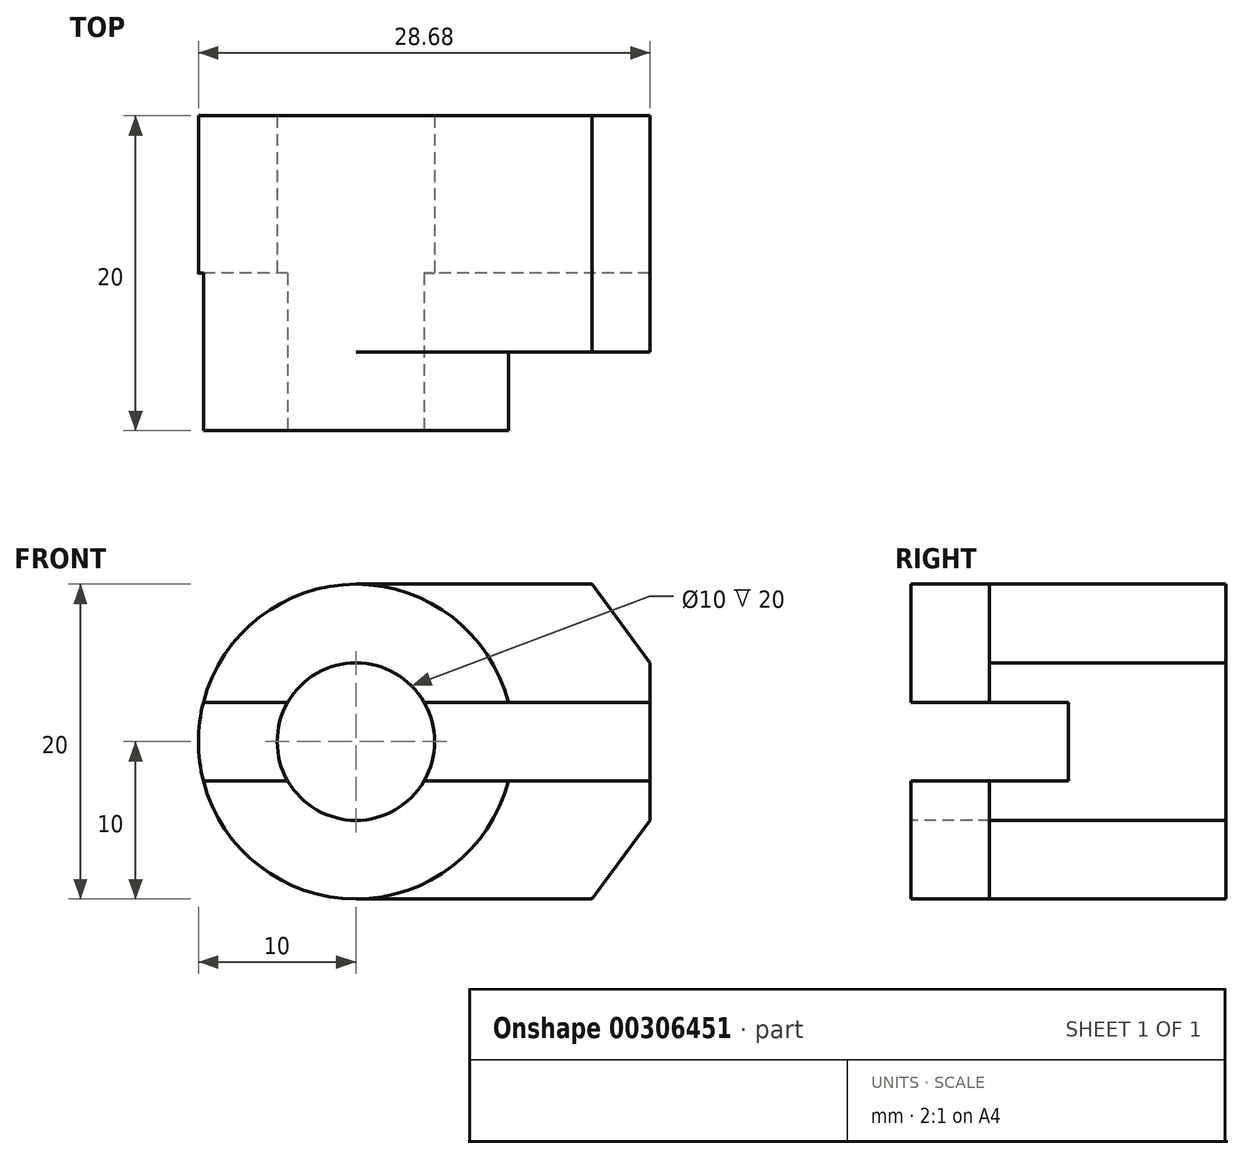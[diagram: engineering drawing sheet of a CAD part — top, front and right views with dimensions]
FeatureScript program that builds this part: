
annotation { "Feature Type Name" : "Feature", "Feature Type Description" : "" }
export const myFeature = defineFeature(function(context is Context, id is Id, definition is map)
    precondition{}
    {
        {
            var Q0;
            Q0=qCreatedBy(makeId("Front.planeOp"),FACE);
            var sketch = newSketch(context, id + "F0", { "sketchPlane" : qUnion([Q0])});
            skCircle(sketch, "E0", {"center": v(0, 0) * mm, "radius": 10 * mm});
            skLineSegment(sketch, "E1", {"start": v(0, 10) * mm, "end": v(15, 10) * mm});
            skLineSegment(sketch, "E2", {"start": v(0, -10) * mm, "end": v(15, -10) * mm});
            skLineSegment(sketch, "E3", {"start": v(15, 10) * mm, "end": v(18.68, 5) * mm});
            skLineSegment(sketch, "E4", {"start": v(18.68, 5) * mm, "end": v(18.68, -5) * mm});
            skLineSegment(sketch, "E5", {"start": v(18.68, -5) * mm, "end": v(15, -10) * mm});
            skSolve(sketch);
        }
        {
            var Q0;
            {var subQ0=sQuery(id+"F0.wireOp",EDGE,"E0");var subQ1=makeQuery(id+"F0.imprint","INTERSECT",VERTEX,{"derivedFrom":[subQ0,sQuery(id+"F0.wireOp",EDGE,"E1")]});Q0=makeQuery(id+"F0.imprint","IMPRINT",FACE,{"disambiguationData":[TD([[makeQuery(id+"F0.imprint","IMPRINT",EDGE,{"disambiguationData":[TD([[subQ1,-1.0]])],"derivedFrom":subQ0}),1.0]])]});}
            extrude(context, id + "F1", {"entities" : qUnion([Q0]), "depth" : 20 * mm});
        }
        {
            var Q0;
            {var subQ1=sQuery(id+"F0.wireOp",EDGE,"E1");Q0=makeQuery(id+"F0.imprint","IMPRINT",FACE,{"disambiguationData":[TD([[makeQuery(id+"F0.imprint","IMPRINT",EDGE,{"derivedFrom":subQ1}),-1.0]])]});}
            extrude(context, id + "F2", {"entities" : qUnion([Q0]), "operationType" : NewBodyOperationType.ADD, "depth" : 15 * mm});
        }
        {
            var Q0;
            Q0=makeQuery(id+"F1.opExtrude","CAP_FACE",FACE,{"disambiguationData":[OSD([sQuery(id+"F0.wireOp",EDGE,"E0")])],"isStart":false});
            var sketch = newSketch(context, id + "F3", { "sketchPlane" : qUnion([Q0])});
            skCircle(sketch, "E6", {"center": v(0, 0) * mm, "radius": 5 * mm});
            skSolve(sketch);
        }
        {
            var Q0;
            Q0=makeQuery(id+"F3.imprint","IMPRINT",FACE,{"disambiguationData":[TD([[makeQuery(id+"F3.imprint","IMPRINT",EDGE,{"derivedFrom":sQuery(id+"F3.wireOp",EDGE,"E6")}),1.0]])]});
            extrude(context, id + "F4", {"entities" : qUnion([Q0]), "operationType" : NewBodyOperationType.REMOVE, "endBound" : BoundingType.THROUGH_ALL, "oppositeDirection" : true, "depth" : 25 * mm});
        }
        {
            var Q0;
            Q0=makeQuery(id+"F1.opExtrude","CAP_FACE",FACE,{"disambiguationData":[OSD([sQuery(id+"F0.wireOp",EDGE,"E0")])],"isStart":false});
            var sketch = newSketch(context, id + "F5", { "sketchPlane" : qUnion([Q0])});
            skLineSegment(sketch, "E7.bottom", {"start": v(18.68, 2.5) * mm, "end": v(-9.68, 2.5) * mm});
            skLineSegment(sketch, "E7.top", {"start": v(18.68, -2.5) * mm, "end": v(-9.68, -2.5) * mm});
            skLineSegment(sketch, "E7.left", {"start": v(18.68, 2.5) * mm, "end": v(18.68, -2.5) * mm});
            skArc(sketch, "E8", {"start": v(-9.68, 2.5) * mm, "mid": v(-10, 0) * mm, "end": v(-9.68, -2.5) * mm});
            skSolve(sketch);
        }
        {
            var Q0;
            {var subQ0=sQuery(id+"F5.wireOp",EDGE,"E7.bottom");var subQ1=makeQuery(id+"F1.opExtrude","CAP_EDGE",EDGE,{"disambiguationData":[OSD([sQuery(id+"F0.wireOp",EDGE,"E0")])],"isStart":false});var subQ2=makeQuery(id+"F5.imprint","INTERSECT",VERTEX,{"derivedFrom":[subQ1,subQ0]});Q0=makeQuery(id+"F5.imprint","IMPRINT",FACE,{"disambiguationData":[TD([[makeQuery(id+"F5.imprint","IMPRINT",EDGE,{"disambiguationData":[TD([[subQ2,-1.0]])],"derivedFrom":subQ0}),1.0]])]});}
            var Q1;
            {var subQ0=sQuery(id+"F5.wireOp",EDGE,"E8");Q1=makeQuery(id+"F5.imprint","IMPRINT",FACE,{"disambiguationData":[TD([[makeQuery(id+"F5.imprint","IMPRINT",EDGE,{"derivedFrom":subQ0}),1.0]])]});}
            extrude(context, id + "F6", {"entities" : qUnion([Q0, Q1]), "operationType" : NewBodyOperationType.REMOVE, "oppositeDirection" : true, "depth" : 10 * mm});
        }
        {
            var Q0;
            {var subQ0=sQuery(id+"F5.wireOp",EDGE,"E7.left");Q0=makeQuery(id+"F5.imprint","IMPRINT",FACE,{"disambiguationData":[TD([[makeQuery(id+"F5.imprint","IMPRINT",EDGE,{"derivedFrom":subQ0}),-1.0]])]});}
            extrude(context, id + "F7", {"entities" : qUnion([Q0]), "operationType" : NewBodyOperationType.REMOVE, "oppositeDirection" : true, "depth" : 10 * mm});
        }
    });
